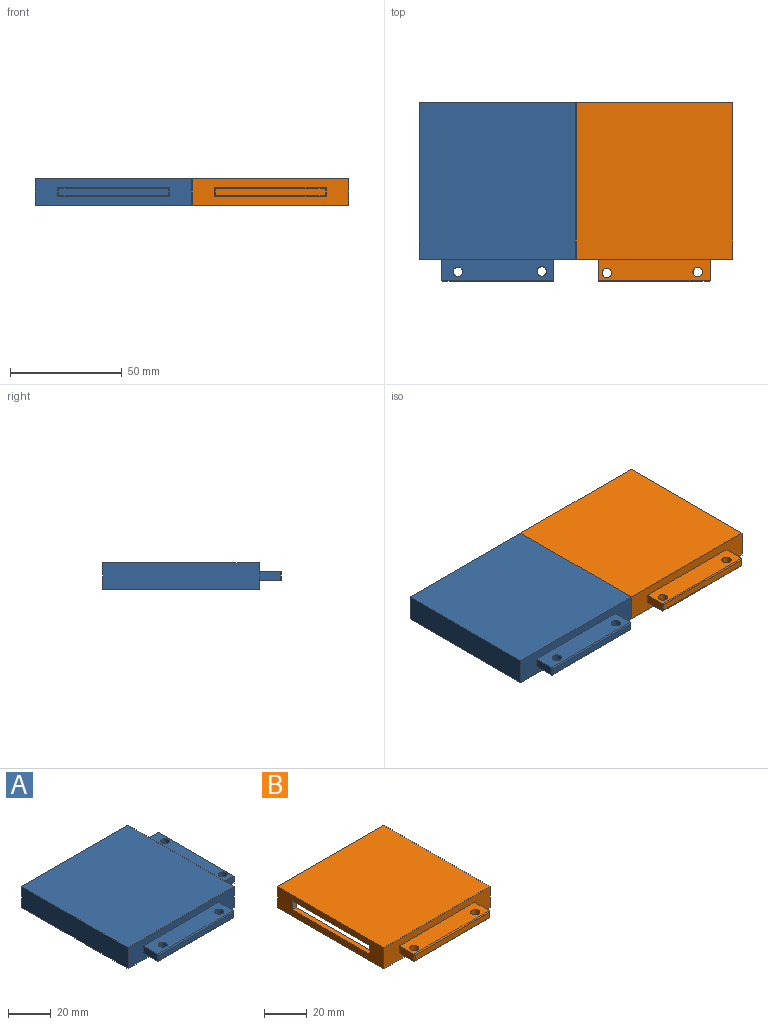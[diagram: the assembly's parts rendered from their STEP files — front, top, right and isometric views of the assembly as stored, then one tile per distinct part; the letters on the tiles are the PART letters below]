
ASSEMBLY  parts=2 mates=1
PART A: 29 faces, bbox 80x80x12 mm
  f0: plane 70x70mm, normal (0,0,-1), area 675mm2, adj f1,f2,f3,f4,f16,f17,f18,f19
  f1: plane 70x12mm, normal (1,0,0), area 640mm2, adj f0,f2,f4,f5,f11,f12,f13,f14
  f2: plane 70x12mm, normal (0,1,0), area 840mm2, adj f0,f1,f3,f5
  f3: plane 70x12mm, normal (-1,0,0), area 840mm2, adj f0,f2,f4,f5
  f4: plane 70x12mm, normal (0,-1,0), area 640mm2, adj f0,f1,f3,f5,f6,f7,f8,f9
  f5: plane 70x70mm, normal (0,0,1), area 4900mm2, adj f1,f2,f3,f4
  f6: plane 50x9.5mm, normal (0,0,1), area 447.2mm2, adj f4,f7,f9,f23,f24,f25
  f7: plane 9.5x4mm, normal (-1,0,0), area 38mm2, adj f4,f6,f8,f26
  f8: plane 50x9.5mm, normal (0,0,-1), area 447.2mm2, adj f4,f7,f9,f23,f24,f28
  f9: plane 9.5x4mm, normal (1,0,0), area 38mm2, adj f4,f6,f8,f27
  f10: plane 49x3mm, normal (0,-1,0), area 147mm2, adj f25,f26,f27,f28
  f11: plane 50x10mm, normal (0,0,1), area 474.9mm2, adj f1,f12,f14,f15,f21,f22
  f12: plane 10x4mm, normal (0,-1,0), area 40mm2, adj f1,f11,f13,f15
  f13: plane 50x10mm, normal (0,0,-1), area 474.9mm2, adj f1,f12,f14,f15,f21,f22
  f14: plane 10x4mm, normal (0,1,0), area 40mm2, adj f1,f11,f13,f15
  f15: plane 50x4mm, normal (1,0,0), area 200mm2, adj f11,f12,f13,f14
  f16: plane 65x9.5mm, normal (-1,0,0), area 617.5mm2, adj f0,f17,f19,f20
  f17: plane 65x9.5mm, normal (0,-1,0), area 617.5mm2, adj f0,f16,f18,f20
  f18: plane 65x9.5mm, normal (1,0,0), area 617.5mm2, adj f0,f17,f19,f20
  f19: plane 65x9.5mm, normal (0,1,0), area 617.5mm2, adj f0,f16,f18,f20
  f20: plane 65x65mm, normal (0,0,-1), area 4225mm2, adj f16,f17,f18,f19
  f21: cylinder r=2mm len=4mm, axis (0,0,1), area 50.3mm2, adj f11,f13
  f22: cylinder r=2mm len=4mm, axis (0,0,1), area 50.3mm2, adj f11,f13
  f23: cylinder r=2.1mm len=4.21mm, axis (0,0,1), area 52.9mm2, adj f6,f8
  f24: cylinder r=2.1mm len=4.21mm, axis (0,0,1), area 52.9mm2, adj f6,f8
  f25: cylinder r=0.5mm len=50mm, axis (1,0,0), area 39mm2, adj f6,f10,f26,f27
  f26: cylinder r=0.5mm len=4mm, axis (0,0,1), area 2.9mm2, adj f7,f10,f25,f28
  f27: cylinder r=0.5mm len=4mm, axis (0,0,-1), area 2.9mm2, adj f9,f10,f25,f28
  f28: cylinder r=0.5mm len=50mm, axis (-1,0,0), area 39mm2, adj f8,f10,f26,f27
PART B: 34 faces, bbox 70x80x12 mm
  f0: plane 70x12mm, normal (-1,0,0), area 585mm2, adj f4,f5,f6,f7,f20,f21,f22,f23
  f1: plane 70x12mm, normal (1,0,0), area 528mm2, adj f4,f5,f6,f7,f26,f27,f28,f29
  f2: plane 65x9.5mm, normal (1,0,0), area 362.5mm2, adj f7,f13,f14,f15,f20,f21,f22,f23
  f3: plane 65x9.5mm, normal (-1,0,0), area 362.5mm2, adj f7,f13,f14,f15,f16,f17,f18,f19
  f4: plane 70x12mm, normal (0,1,0), area 840mm2, adj f0,f1,f6,f7
  f5: plane 70x12mm, normal (0,-1,0), area 640mm2, adj f0,f1,f6,f7,f8,f9,f10,f11
  f6: plane 70x70mm, normal (0,0,1), area 4900mm2, adj f0,f1,f4,f5
  f7: plane 70x70mm, normal (0,0,-1), area 675mm2, adj f0,f1,f2,f3,f4,f5,f13,f14
  f8: plane 50x9.5mm, normal (0,0,1), area 447.2mm2, adj f5,f9,f11,f24,f25,f31
  f9: plane 9.5x4mm, normal (1,0,0), area 38mm2, adj f5,f8,f10,f30
  f10: plane 50x9.5mm, normal (0,0,-1), area 447.2mm2, adj f5,f9,f11,f24,f25,f32
  f11: plane 9.5x4mm, normal (-1,0,0), area 38mm2, adj f5,f8,f10,f33
  f12: plane 49x3mm, normal (0,-1,0), area 147mm2, adj f30,f31,f32,f33
  f13: plane 65x9.5mm, normal (0,-1,0), area 617.5mm2, adj f2,f3,f7,f15
  f14: plane 65x9.5mm, normal (0,1,0), area 617.5mm2, adj f2,f3,f7,f15
  f15: plane 65x65mm, normal (0,0,-1), area 4225mm2, adj f2,f3,f13,f14
  f16: plane 5x2mm, normal (0,1,0), area 10mm2, adj f3,f17,f19,f28
  f17: plane 51x2mm, normal (0,0,1), area 102mm2, adj f3,f16,f18,f26
  f18: plane 5x2mm, normal (0,-1,0), area 10mm2, adj f3,f17,f19,f27
  f19: plane 51x2mm, normal (0,0,-1), area 102mm2, adj f3,f16,f18,f29
  f20: plane 51x2.5mm, normal (0,0,-1), area 127.5mm2, adj f0,f2,f21,f23
  f21: plane 5x2.5mm, normal (0,-1,0), area 12.5mm2, adj f0,f2,f20,f22
  f22: plane 51x2.5mm, normal (0,0,1), area 127.5mm2, adj f0,f2,f21,f23
  f23: plane 5x2.5mm, normal (0,1,0), area 12.5mm2, adj f0,f2,f20,f22
  f24: cylinder r=2.1mm len=4.21mm, axis (0,0,1), area 52.9mm2, adj f8,f10
  f25: cylinder r=2.1mm len=4.21mm, axis (0,0,1), area 52.9mm2, adj f8,f10
  f26: cylinder r=0.5mm len=52mm, axis (0,-1,0), area 40.3mm2, adj f1,f17,f27,f28
  f27: cylinder r=0.5mm len=6mm, axis (0,0,-1), area 4.2mm2, adj f1,f18,f26,f29
  f28: cylinder r=0.5mm len=6mm, axis (0,0,1), area 4.2mm2, adj f1,f16,f26,f29
  f29: cylinder r=0.5mm len=52mm, axis (0,1,0), area 40.3mm2, adj f1,f19,f27,f28
  f30: cylinder r=0.5mm len=4mm, axis (0,0,1), area 2.9mm2, adj f9,f12,f31,f32
  f31: cylinder r=0.5mm len=50mm, axis (-1,0,0), area 39mm2, adj f8,f12,f30,f33
  f32: cylinder r=0.5mm len=50mm, axis (1,0,0), area 39mm2, adj f10,f12,f30,f33
  f33: cylinder r=0.5mm len=4mm, axis (0,0,-1), area 2.9mm2, adj f11,f12,f31,f32
PLACE A t=(-24.1,-55.18,30.12)mm fixed
PLACE B t=(-34.3,-55.18,30.12)mm
MATE pin_slot A.f1 <-> B.f0  axis (1,0,0) through (-23.1,-8.62,36.12)mm
